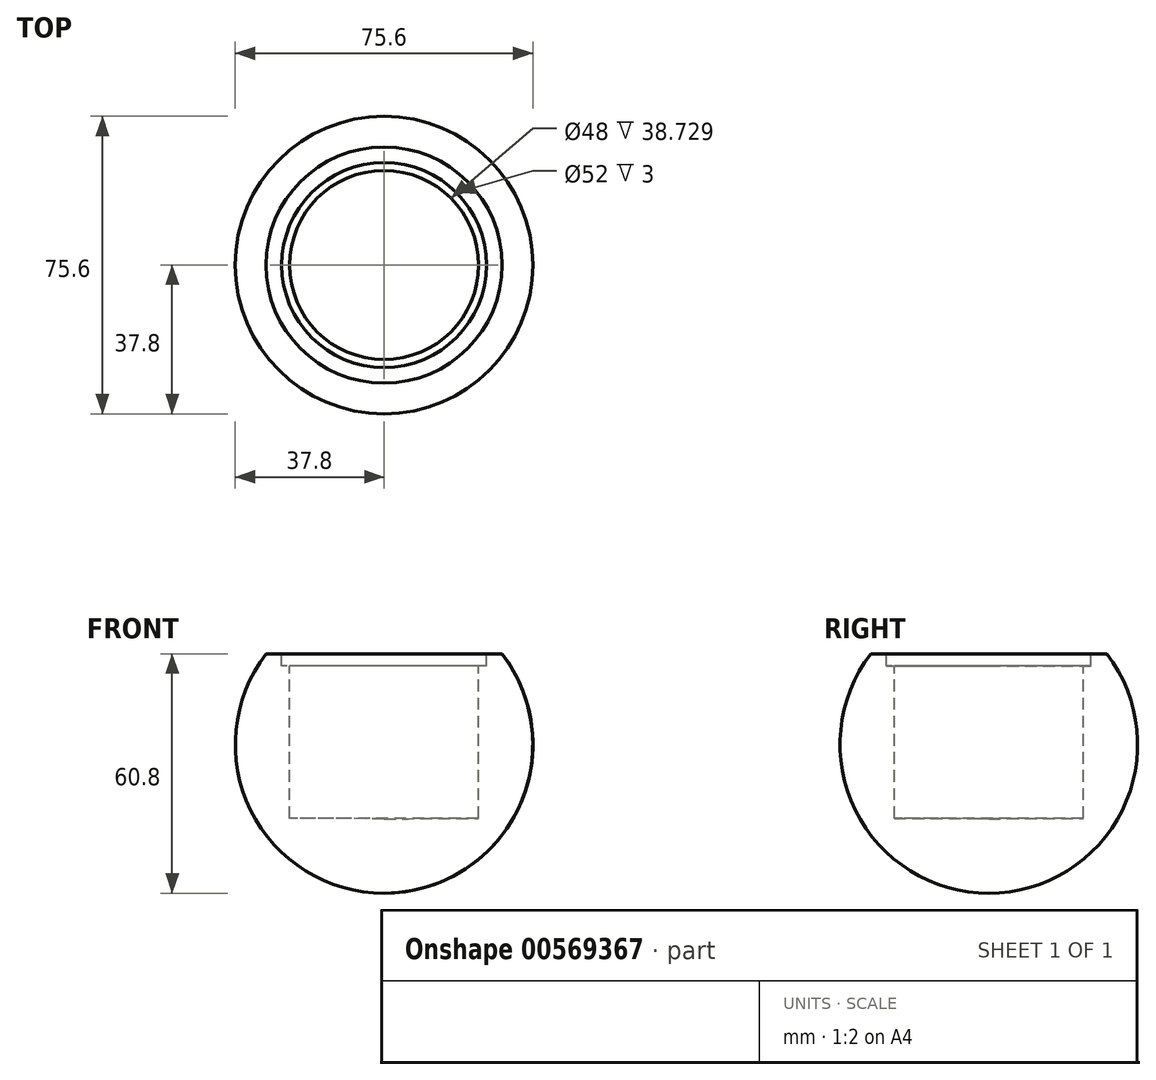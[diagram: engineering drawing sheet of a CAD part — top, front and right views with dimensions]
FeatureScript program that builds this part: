
annotation { "Feature Type Name" : "Feature", "Feature Type Description" : "" }
export const myFeature = defineFeature(function(context is Context, id is Id, definition is map)
    precondition{}
    {
        {
            var Q0;
            Q0=qCreatedBy(makeId("Front.planeOp"),FACE);
            var sketch = newSketch(context, id + "F0", { "sketchPlane" : qUnion([Q0])});
            skLineSegment(sketch, "E0", {"start": v(26, 23) * mm, "end": v(26, 20) * mm});
            skLineSegment(sketch, "E1", {"start": v(26, 20) * mm, "end": v(24, 20) * mm});
            skArc(sketch, "E2", {"start": v(0, -37.8) * mm, "mid": v(17.9, -33.3) * mm, "end": v(31.52, -20.87) * mm});
            skLineSegment(sketch, "E3", {"start": v(26, 23) * mm, "end": v(30, 23) * mm});
            skLineSegment(sketch, "E4", {"start": v(0, 0) * mm, "end": v(0, -37.8) * mm, "construction": true});
            skLineSegment(sketch, "E5", {"start": v(0, 0) * mm, "end": v(0, -37.8) * mm});
            skPoint(sketch, "E6.orphan", {"position": v(0, 103.81) * mm});
            skLineSegment(sketch, "E7", {"start": v(0, 71.04) * mm, "end": v(0, 0) * mm, "construction": true});
            skLineSegment(sketch, "E8", {"start": v(24, -18.73) * mm, "end": v(0, -18.9) * mm});
            skLineSegment(sketch, "E9.trimOffspring", {"start": v(0, -18.9) * mm, "end": v(0, -44.64) * mm, "construction": true});
            skPoint(sketch, "E10.start.orphan", {"position": v(24, 0) * mm});
            skLineSegment(sketch, "E11", {"start": v(24, 20) * mm, "end": v(24, -11.04) * mm});
            skArc(sketch, "E12.trimOffspring", {"start": v(33.9, -16.73) * mm, "mid": v(37.62, 3.7) * mm, "end": v(30, 23) * mm});
            skLineSegment(sketch, "E13.trimOffspring", {"start": v(24, -16.55) * mm, "end": v(24, -18.73) * mm});
            skLineSegment(sketch, "E14", {"start": v(24, -11.04) * mm, "end": v(24, -16.55) * mm});
            skArc(sketch, "E15", {"start": v(0, -37.8) * mm, "mid": v(33.9, -16.73) * mm, "end": v(30, 23) * mm});
            skSolve(sketch);
        }
        {
            var Q0;
            Q0=makeQuery(id+"F0.imprint","IMPRINT",FACE,{"disambiguationData":[TD([[makeQuery(id+"F0.imprint","IMPRINT",EDGE,{"derivedFrom":sQuery(id+"F0.wireOp",EDGE,"E0")}),1.0]])]});
            var Q1;
            Q1=sQuery(id+"F0.wireOp",EDGE,"E7");
            revolve(context, id + "F1", {"entities" : qUnion([Q0]), "axis" : qUnion([Q1]), "revolveType" : RevolveType.FULL});
        }
    });
